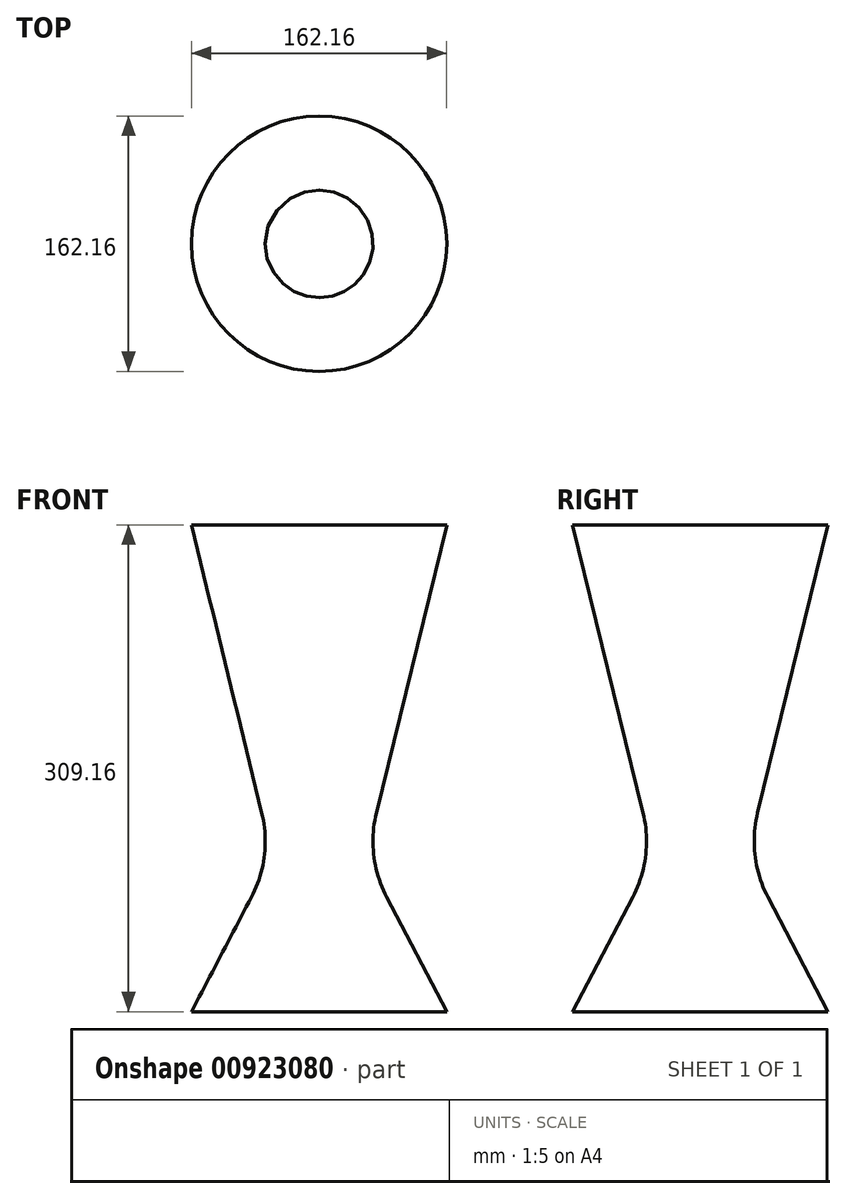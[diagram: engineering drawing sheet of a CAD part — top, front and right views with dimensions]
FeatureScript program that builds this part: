
annotation { "Feature Type Name" : "Feature", "Feature Type Description" : "" }
export const myFeature = defineFeature(function(context is Context, id is Id, definition is map)
    precondition{}
    {
        {
            var Q0;
            Q0=qCreatedBy(makeId("Front.planeOp"),FACE);
            var sketch = newSketch(context, id + "F0", { "sketchPlane" : qUnion([Q0])});
            skLineSegment(sketch, "E0", {"start": v(81.08, 210.84) * mm, "end": v(36.4, 27.96) * mm});
            skLineSegment(sketch, "E1", {"start": v(42.92, -25.5) * mm, "end": v(81.08, -98.32) * mm});
            skPoint(sketch, "E2.visualSharp", {"position": v(29.56, 0) * mm});
            skArc(sketch, "E2.filletArc", {"start": v(36.4, 27.96) * mm, "mid": v(34.78, 0.64) * mm, "end": v(42.92, -25.5) * mm});
            skLineSegment(sketch, "E3", {"start": v(0, 210.84) * mm, "end": v(0, -98.32) * mm, "construction": true});
            skSolve(sketch);
        }
        {
            var Q0;
            Q0 = qSketchRegion(id + "F0", true);
            var Q1;
            Q1=sQuery(id+"F0.wireOp",EDGE,"E0");
            var Q2;
            Q2=sQuery(id+"F0.wireOp",EDGE,"E2.filletArc");
            var Q3;
            Q3=sQuery(id+"F0.wireOp",EDGE,"E1");
            var Q4;
            Q4=sQuery(id+"F0.wireOp",EDGE,"E3");
            revolve(context, id + "F1", {"bodyType" : ToolBodyType.SURFACE, "surfaceOperationType" : NewSurfaceOperationType.NEW, "entities" : qUnion([Q0]), "surfaceEntities" : qUnion([Q1, Q2, Q3]), "axis" : qUnion([Q4]), "revolveType" : RevolveType.FULL});
        }
    });
